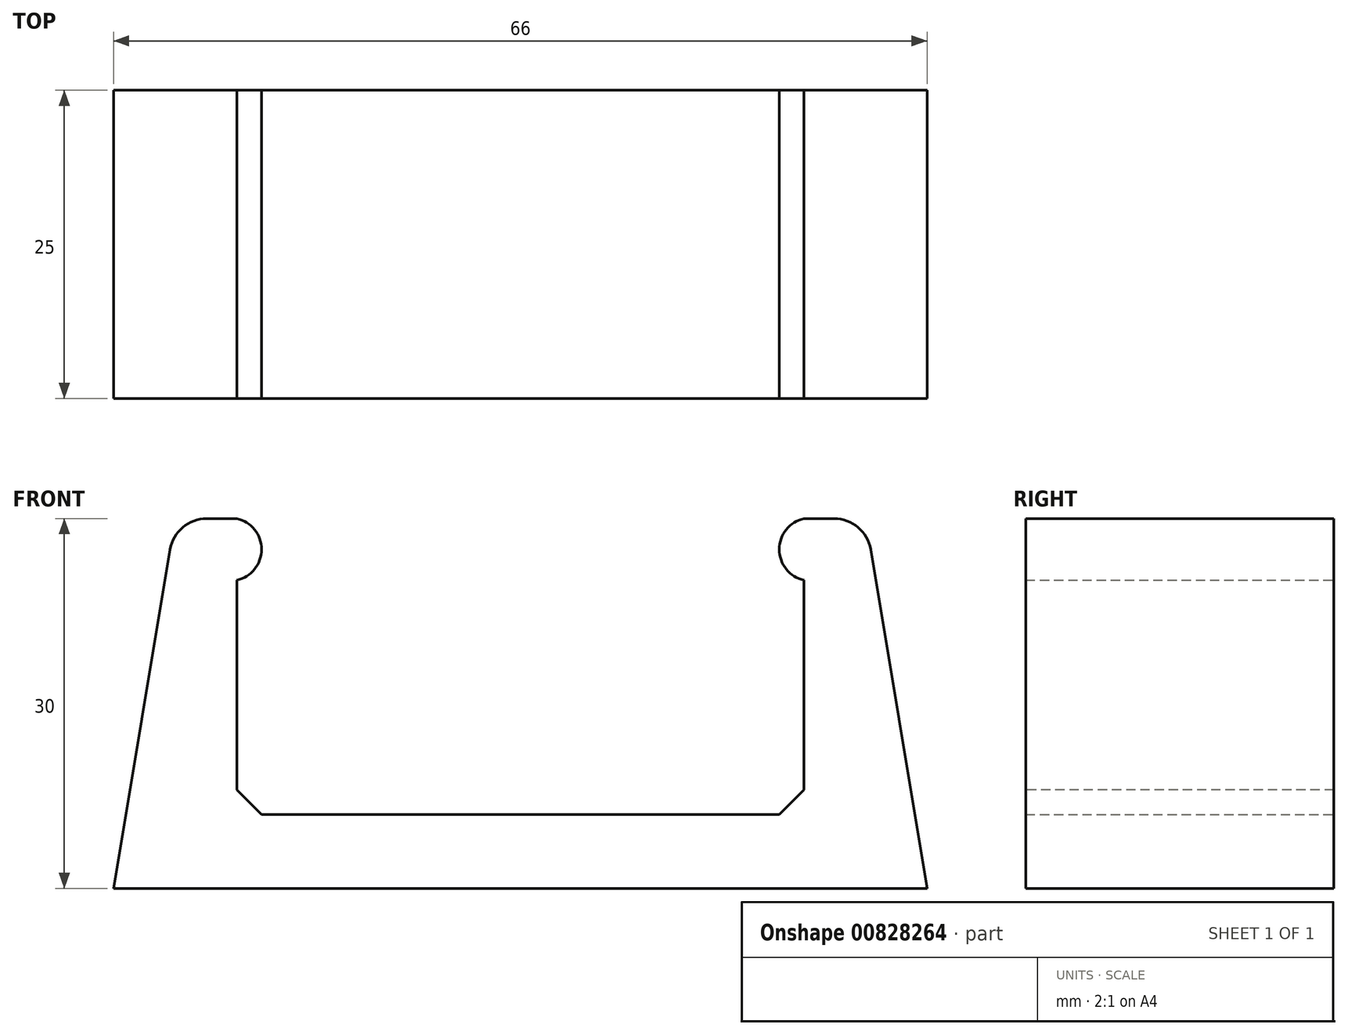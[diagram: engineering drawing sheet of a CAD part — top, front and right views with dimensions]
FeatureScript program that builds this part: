
annotation { "Feature Type Name" : "Feature", "Feature Type Description" : "" }
export const myFeature = defineFeature(function(context is Context, id is Id, definition is map)
    precondition{}
    {
        {
            var Q0;
            Q0=qCreatedBy(makeId("Front.planeOp"),FACE);
            var sketch = newSketch(context, id + "F0", { "sketchPlane" : qUnion([Q0])});
            skLineSegment(sketch, "E0.bottom", {"start": v(-10, 0) * mm, "end": v(56, 0) * mm});
            skLineSegment(sketch, "E0.top", {"start": v(-10, 30) * mm, "end": v(56, 30) * mm});
            skLineSegment(sketch, "E0.left", {"start": v(-10, 0) * mm, "end": v(-10, 30) * mm});
            skLineSegment(sketch, "E0.right", {"start": v(56, 0) * mm, "end": v(56, 30) * mm});
            skLineSegment(sketch, "E1", {"start": v(-10, 0) * mm, "end": v(-5, 30) * mm});
            skLineSegment(sketch, "E2", {"start": v(-5, 30) * mm, "end": v(51, 30) * mm});
            skLineSegment(sketch, "E3", {"start": v(51, 30) * mm, "end": v(56, 0) * mm});
            skLineSegment(sketch, "E4.bottom", {"start": v(0, 30) * mm, "end": v(46, 30) * mm});
            skLineSegment(sketch, "E4.top", {"start": v(0, 6) * mm, "end": v(46, 6) * mm});
            skLineSegment(sketch, "E4.left", {"start": v(0, 30) * mm, "end": v(0, 6) * mm});
            skLineSegment(sketch, "E4.right", {"start": v(46, 30) * mm, "end": v(46, 6) * mm});
            skArc(sketch, "E5", {"start": v(46, 30) * mm, "mid": v(44, 27.5) * mm, "end": v(46, 25) * mm});
            skArc(sketch, "E6", {"start": v(0, 25) * mm, "mid": v(2, 27.5) * mm, "end": v(0, 30) * mm});
            skSolve(sketch);
        }
        {
            var Q0;
            Q0=makeQuery(id+"F0.imprint","IMPRINT",FACE,{"disambiguationData":[TD([[makeQuery(id+"F0.imprint","IMPRINT",EDGE,{"derivedFrom":sQuery(id+"F0.wireOp",EDGE,"E0.bottom")}),1.0]])]});
            var Q1;
            {var subQ0=sQuery(id+"F0.wireOp",EDGE,"E6");Q1=makeQuery(id+"F0.imprint","IMPRINT",FACE,{"disambiguationData":[TD([[makeQuery(id+"F0.imprint","IMPRINT",EDGE,{"derivedFrom":subQ0}),1.0]])]});}
            var Q2;
            {var subQ0=sQuery(id+"F0.wireOp",EDGE,"E5");Q2=makeQuery(id+"F0.imprint","IMPRINT",FACE,{"disambiguationData":[TD([[makeQuery(id+"F0.imprint","IMPRINT",EDGE,{"derivedFrom":subQ0}),1.0]])]});}
            extrude(context, id + "F1", {"entities" : qUnion([Q0, Q1, Q2]), "depth" : 25 * mm, "offsetDistance" : 25 * mm});
        }
        {
            var Q0;
            Q0=makeQuery(id+"F1.opExtrude","SWEPT_EDGE",EDGE,{"disambiguationData":[OSD([sQuery(id+"F0.wireOp",EDGE,"E4.top"),sQuery(id+"F0.wireOp",EDGE,"E4.right")])]});
            var Q1;
            Q1=makeQuery(id+"F1.opExtrude","SWEPT_EDGE",EDGE,{"disambiguationData":[OSD([sQuery(id+"F0.wireOp",EDGE,"E4.top"),sQuery(id+"F0.wireOp",EDGE,"E4.left")])]});
            chamfer(context, id + "F2", {"entities" : qUnion([Q0, Q1]), "width" : 2 * mm, "tangentPropagation" : true});
        }
        {
            var Q0;
            Q0=makeQuery(id+"F1.opExtrude","SWEPT_EDGE",EDGE,{"disambiguationData":[OSD([sQuery(id+"F0.wireOp",EDGE,"E0.top"),sQuery(id+"F0.wireOp",EDGE,"E2"),sQuery(id+"F0.wireOp",EDGE,"E3")])]});
            var Q1;
            Q1=makeQuery(id+"F1.opExtrude","SWEPT_EDGE",EDGE,{"disambiguationData":[OSD([sQuery(id+"F0.wireOp",EDGE,"E0.top"),sQuery(id+"F0.wireOp",EDGE,"E1"),sQuery(id+"F0.wireOp",EDGE,"E2")])]});
            fillet(context, id + "F3", {"entities" : qUnion([Q0, Q1]), "radius" : 3 * mm, "tangentPropagation" : true, "allowEdgeOverflow" : false});
        }
    });
